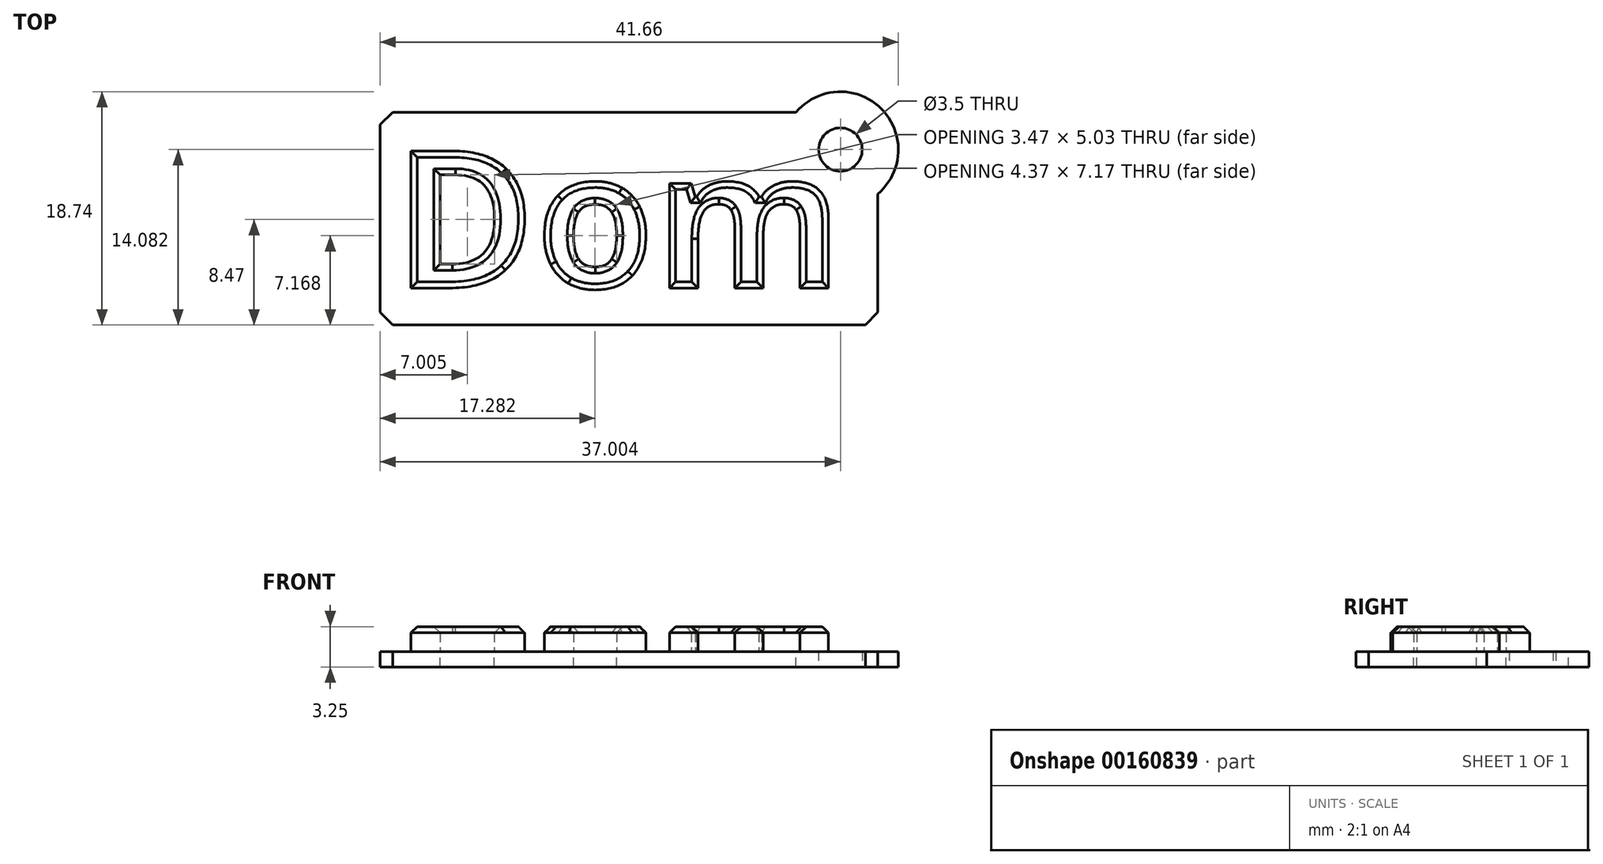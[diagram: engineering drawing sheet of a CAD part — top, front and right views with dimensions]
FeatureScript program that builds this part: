
annotation { "Feature Type Name" : "Feature", "Feature Type Description" : "" }
export const myFeature = defineFeature(function(context is Context, id is Id, definition is map)
    precondition{}
    {
        {
            var Q0;
            Q0=qCreatedBy(makeId("Top.planeOp"),FACE);
            var sketch = newSketch(context, id + "F0", { "sketchPlane" : qUnion([Q0])});
            skLineSegment(sketch, "E0.bottom", {"start": v(-3.85, 4.54) * mm, "end": v(36.15, 4.54) * mm});
            skLineSegment(sketch, "E0.left", {"start": v(-3.85, 4.54) * mm, "end": v(-3.85, -12.54) * mm});
            skLineSegment(sketch, "E0.right", {"start": v(36.15, 4.54) * mm, "end": v(36.15, -12.54) * mm});
            skText(sketch, "E1", { "text": "Dom", "fontName": "OpenSans-Bold.ttf"});
            skLineSegment(sketch, "E2", {"start": v(-3.85, -12.54) * mm, "end": v(36.15, -12.54) * mm});
            skPoint(sketch, "E3", {"position": v(33.15, 1.54) * mm});
            skArc(sketch, "E4", {"start": v(36.15, -2.02) * mm, "mid": v(36.45, 4.83) * mm, "end": v(29.6, 4.54) * mm});
            const initialGuessF0  = {"E1": [-0.00275, -0.00958, 1, 0, 0.0111]};
            skSetInitialGuess(sketch, initialGuessF0);
            skSolve(sketch);
        }
        {
            var Q0;
            Q0=makeQuery(id+"F0.imprint","IMPRINT",FACE,{"disambiguationData":[TD([[makeQuery(id+"F0.imprint","IMPRINT",EDGE,{"derivedFrom":sQuery(id+"F0.wireOp",EDGE,"E1.sketch_text.stroke-0")}),-1.0]])]});
            var Q1;
            Q1=makeQuery(id+"F0.imprint","IMPRINT",FACE,{"disambiguationData":[TD([[makeQuery(id+"F0.imprint","IMPRINT",EDGE,{"derivedFrom":sQuery(id+"F0.wireOp",EDGE,"E1.sketch_text.stroke-12")}),-1.0]])]});
            var Q2;
            Q2=makeQuery(id+"F0.imprint","IMPRINT",FACE,{"disambiguationData":[TD([[makeQuery(id+"F0.imprint","IMPRINT",EDGE,{"derivedFrom":sQuery(id+"F0.wireOp",EDGE,"E1.sketch_text.stroke-30")}),-1.0]])]});
            extrude(context, id + "F1", {"entities" : qUnion([Q0, Q1, Q2]), "depth" : 2 * mm});
        }
        {
            var Q0;
            Q0=makeQuery(id+"F0.imprint","IMPRINT",FACE,{"disambiguationData":[TD([[makeQuery(id+"F0.imprint","IMPRINT",EDGE,{"derivedFrom":sQuery(id+"F0.wireOp",EDGE,"E0.bottom")}),-1.0]])]});
            var Q1;
            Q1=makeQuery(id+"F0.imprint","IMPRINT",FACE,{"disambiguationData":[TD([[makeQuery(id+"F0.imprint","IMPRINT",EDGE,{"derivedFrom":sQuery(id+"F0.wireOp",EDGE,"E1.sketch_text.stroke-0")}),-1.0]])]});
            var Q2;
            Q2=makeQuery(id+"F0.imprint","IMPRINT",FACE,{"disambiguationData":[TD([[makeQuery(id+"F0.imprint","IMPRINT",EDGE,{"derivedFrom":sQuery(id+"F0.wireOp",EDGE,"E1.sketch_text.stroke-12")}),-1.0]])]});
            var Q3;
            Q3=makeQuery(id+"F0.imprint","IMPRINT",FACE,{"disambiguationData":[TD([[makeQuery(id+"F0.imprint","IMPRINT",EDGE,{"derivedFrom":sQuery(id+"F0.wireOp",EDGE,"E1.sketch_text.stroke-30")}),-1.0]])]});
            var Q4;
            {var subQ3=sQuery(id+"F0.wireOp",EDGE,"E4");Q4=makeQuery(id+"F0.imprint","IMPRINT",FACE,{"disambiguationData":[TD([[makeQuery(id+"F0.imprint","IMPRINT",EDGE,{"derivedFrom":subQ3}),1.0]])]});}
            extrude(context, id + "F2", {"entities" : qUnion([Q0, Q1, Q2, Q3, Q4]), "oppositeDirection" : true, "depth" : 1.25 * mm});
        }
        {
            var Q0;
            Q0=sQuery(id+"F0.wireOp",VERTEX,"E3");
            var Q1;
            Q1=makeQuery(id+"F2.opExtrude","SWEPT_BODY",BODY,{"disambiguationData":[OSD([sQuery(id+"F0.wireOp",EDGE,"E0.bottom"),sQuery(id+"F0.wireOp",EDGE,"E0.left"),sQuery(id+"F0.wireOp",EDGE,"E0.right"),sQuery(id+"F0.wireOp",EDGE,"E1.sketch_text.stroke-0"),sQuery(id+"F0.wireOp",EDGE,"E1.sketch_text.stroke-1"),sQuery(id+"F0.wireOp",EDGE,"E1.sketch_text.stroke-2"),sQuery(id+"F0.wireOp",EDGE,"E1.sketch_text.stroke-3"),sQuery(id+"F0.wireOp",EDGE,"E1.sketch_text.stroke-4"),sQuery(id+"F0.wireOp",EDGE,"E1.sketch_text.stroke-5"),sQuery(id+"F0.wireOp",EDGE,"E1.sketch_text.stroke-6"),sQuery(id+"F0.wireOp",EDGE,"E1.sketch_text.stroke-20"),sQuery(id+"F0.wireOp",EDGE,"E1.sketch_text.stroke-21"),sQuery(id+"F0.wireOp",EDGE,"E1.sketch_text.stroke-22"),sQuery(id+"F0.wireOp",EDGE,"E1.sketch_text.stroke-23"),sQuery(id+"F0.wireOp",EDGE,"E1.sketch_text.stroke-24"),sQuery(id+"F0.wireOp",EDGE,"E1.sketch_text.stroke-25"),sQuery(id+"F0.wireOp",EDGE,"E1.sketch_text.stroke-26"),sQuery(id+"F0.wireOp",EDGE,"E1.sketch_text.stroke-27"),sQuery(id+"F0.wireOp",EDGE,"E1.sketch_text.stroke-28"),sQuery(id+"F0.wireOp",EDGE,"E1.sketch_text.stroke-29"),sQuery(id+"F0.wireOp",EDGE,"E1.sketch_text.stroke-30"),sQuery(id+"F0.wireOp",EDGE,"E1.sketch_text.stroke-31"),sQuery(id+"F0.wireOp",EDGE,"E1.sketch_text.stroke-32"),sQuery(id+"F0.wireOp",EDGE,"E1.sketch_text.stroke-33"),sQuery(id+"F0.wireOp",EDGE,"E1.sketch_text.stroke-34"),sQuery(id+"F0.wireOp",EDGE,"E1.sketch_text.stroke-35"),sQuery(id+"F0.wireOp",EDGE,"E1.sketch_text.stroke-36"),sQuery(id+"F0.wireOp",EDGE,"E1.sketch_text.stroke-37"),sQuery(id+"F0.wireOp",EDGE,"E1.sketch_text.stroke-38"),sQuery(id+"F0.wireOp",EDGE,"E1.sketch_text.stroke-39"),sQuery(id+"F0.wireOp",EDGE,"E1.sketch_text.stroke-40"),sQuery(id+"F0.wireOp",EDGE,"E1.sketch_text.stroke-41"),sQuery(id+"F0.wireOp",EDGE,"E1.sketch_text.stroke-42"),sQuery(id+"F0.wireOp",EDGE,"E1.sketch_text.stroke-43"),sQuery(id+"F0.wireOp",EDGE,"E1.sketch_text.stroke-44"),sQuery(id+"F0.wireOp",EDGE,"E1.sketch_text.stroke-45"),sQuery(id+"F0.wireOp",EDGE,"E1.sketch_text.stroke-46"),sQuery(id+"F0.wireOp",EDGE,"E1.sketch_text.stroke-47"),sQuery(id+"F0.wireOp",EDGE,"E1.sketch_text.stroke-48"),sQuery(id+"F0.wireOp",EDGE,"E1.sketch_text.stroke-49"),sQuery(id+"F0.wireOp",EDGE,"E1.sketch_text.stroke-50"),sQuery(id+"F0.wireOp",EDGE,"E1.sketch_text.stroke-51"),sQuery(id+"F0.wireOp",EDGE,"E1.sketch_text.stroke-52"),sQuery(id+"F0.wireOp",EDGE,"E1.sketch_text.stroke-53"),sQuery(id+"F0.wireOp",EDGE,"E1.sketch_text.stroke-54"),sQuery(id+"F0.wireOp",EDGE,"E1.sketch_text.stroke-55"),sQuery(id+"F0.wireOp",EDGE,"E1.sketch_text.stroke-56"),sQuery(id+"F0.wireOp",EDGE,"E1.sketch_text.stroke-57"),sQuery(id+"F0.wireOp",EDGE,"E2")])]});
            hole(context, id + "F3", {"style" : HoleStyle.SIMPLE, "endStyle" : HoleEndStyle.BLIND, "holeDiameter" : 3.5 * mm, "holeDepth" : 20 * mm, "locations" : qUnion([Q0]), "scope" : qUnion([Q1]), "startStyle" : HoleStartStyle.PART});
        }
        {
            var Q0;
            Q0=makeQuery(id+"F2.opExtrude","SWEPT_EDGE",EDGE,{"disambiguationData":[OSD([sQuery(id+"F0.wireOp",EDGE,"E0.bottom"),sQuery(id+"F0.wireOp",EDGE,"E0.left")])]});
            var Q1;
            Q1=makeQuery(id+"F2.opExtrude","SWEPT_EDGE",EDGE,{"disambiguationData":[OSD([sQuery(id+"F0.wireOp",EDGE,"E0.left"),sQuery(id+"F0.wireOp",EDGE,"E2")])]});
            var Q2;
            Q2=makeQuery(id+"F2.opExtrude","SWEPT_EDGE",EDGE,{"disambiguationData":[OSD([sQuery(id+"F0.wireOp",EDGE,"E0.right"),sQuery(id+"F0.wireOp",EDGE,"E2")])]});
            chamfer(context, id + "F4", {"entities" : qUnion([Q0, Q1, Q2]), "width" : 1 * mm, "tangentPropagation" : true});
        }
        {
            var Q0;
            Q0=makeQuery(id+"F1.opExtrude","CAP_FACE",FACE,{"disambiguationData":[OSD([sQuery(id+"F0.wireOp",EDGE,"E1.sketch_text.stroke-0"),sQuery(id+"F0.wireOp",EDGE,"E1.sketch_text.stroke-1"),sQuery(id+"F0.wireOp",EDGE,"E1.sketch_text.stroke-2"),sQuery(id+"F0.wireOp",EDGE,"E1.sketch_text.stroke-3"),sQuery(id+"F0.wireOp",EDGE,"E1.sketch_text.stroke-4"),sQuery(id+"F0.wireOp",EDGE,"E1.sketch_text.stroke-5"),sQuery(id+"F0.wireOp",EDGE,"E1.sketch_text.stroke-6"),sQuery(id+"F0.wireOp",EDGE,"E1.sketch_text.stroke-7"),sQuery(id+"F0.wireOp",EDGE,"E1.sketch_text.stroke-8"),sQuery(id+"F0.wireOp",EDGE,"E1.sketch_text.stroke-9"),sQuery(id+"F0.wireOp",EDGE,"E1.sketch_text.stroke-10"),sQuery(id+"F0.wireOp",EDGE,"E1.sketch_text.stroke-11")])],"isStart":false});
            var Q1;
            Q1=makeQuery(id+"F1.opExtrude","CAP_FACE",FACE,{"disambiguationData":[OSD([sQuery(id+"F0.wireOp",EDGE,"E1.sketch_text.stroke-12"),sQuery(id+"F0.wireOp",EDGE,"E1.sketch_text.stroke-13"),sQuery(id+"F0.wireOp",EDGE,"E1.sketch_text.stroke-14"),sQuery(id+"F0.wireOp",EDGE,"E1.sketch_text.stroke-15"),sQuery(id+"F0.wireOp",EDGE,"E1.sketch_text.stroke-16"),sQuery(id+"F0.wireOp",EDGE,"E1.sketch_text.stroke-17"),sQuery(id+"F0.wireOp",EDGE,"E1.sketch_text.stroke-18"),sQuery(id+"F0.wireOp",EDGE,"E1.sketch_text.stroke-19"),sQuery(id+"F0.wireOp",EDGE,"E1.sketch_text.stroke-20"),sQuery(id+"F0.wireOp",EDGE,"E1.sketch_text.stroke-21"),sQuery(id+"F0.wireOp",EDGE,"E1.sketch_text.stroke-22"),sQuery(id+"F0.wireOp",EDGE,"E1.sketch_text.stroke-23"),sQuery(id+"F0.wireOp",EDGE,"E1.sketch_text.stroke-24"),sQuery(id+"F0.wireOp",EDGE,"E1.sketch_text.stroke-25"),sQuery(id+"F0.wireOp",EDGE,"E1.sketch_text.stroke-26"),sQuery(id+"F0.wireOp",EDGE,"E1.sketch_text.stroke-27"),sQuery(id+"F0.wireOp",EDGE,"E1.sketch_text.stroke-28"),sQuery(id+"F0.wireOp",EDGE,"E1.sketch_text.stroke-29")])],"isStart":false});
            var Q2;
            Q2=makeQuery(id+"F1.opExtrude","CAP_FACE",FACE,{"disambiguationData":[OSD([sQuery(id+"F0.wireOp",EDGE,"E1.sketch_text.stroke-30"),sQuery(id+"F0.wireOp",EDGE,"E1.sketch_text.stroke-31"),sQuery(id+"F0.wireOp",EDGE,"E1.sketch_text.stroke-32"),sQuery(id+"F0.wireOp",EDGE,"E1.sketch_text.stroke-33"),sQuery(id+"F0.wireOp",EDGE,"E1.sketch_text.stroke-34"),sQuery(id+"F0.wireOp",EDGE,"E1.sketch_text.stroke-35"),sQuery(id+"F0.wireOp",EDGE,"E1.sketch_text.stroke-36"),sQuery(id+"F0.wireOp",EDGE,"E1.sketch_text.stroke-37"),sQuery(id+"F0.wireOp",EDGE,"E1.sketch_text.stroke-38"),sQuery(id+"F0.wireOp",EDGE,"E1.sketch_text.stroke-39"),sQuery(id+"F0.wireOp",EDGE,"E1.sketch_text.stroke-40"),sQuery(id+"F0.wireOp",EDGE,"E1.sketch_text.stroke-41"),sQuery(id+"F0.wireOp",EDGE,"E1.sketch_text.stroke-42"),sQuery(id+"F0.wireOp",EDGE,"E1.sketch_text.stroke-43"),sQuery(id+"F0.wireOp",EDGE,"E1.sketch_text.stroke-44"),sQuery(id+"F0.wireOp",EDGE,"E1.sketch_text.stroke-45"),sQuery(id+"F0.wireOp",EDGE,"E1.sketch_text.stroke-46"),sQuery(id+"F0.wireOp",EDGE,"E1.sketch_text.stroke-47"),sQuery(id+"F0.wireOp",EDGE,"E1.sketch_text.stroke-48"),sQuery(id+"F0.wireOp",EDGE,"E1.sketch_text.stroke-49"),sQuery(id+"F0.wireOp",EDGE,"E1.sketch_text.stroke-50"),sQuery(id+"F0.wireOp",EDGE,"E1.sketch_text.stroke-51"),sQuery(id+"F0.wireOp",EDGE,"E1.sketch_text.stroke-52"),sQuery(id+"F0.wireOp",EDGE,"E1.sketch_text.stroke-53"),sQuery(id+"F0.wireOp",EDGE,"E1.sketch_text.stroke-54"),sQuery(id+"F0.wireOp",EDGE,"E1.sketch_text.stroke-55"),sQuery(id+"F0.wireOp",EDGE,"E1.sketch_text.stroke-56"),sQuery(id+"F0.wireOp",EDGE,"E1.sketch_text.stroke-57")])],"isStart":false});
            chamfer(context, id + "F5", {"entities" : qUnion([Q0, Q1, Q2]), "width" : 0.5 * mm, "tangentPropagation" : true});
        }
    });
